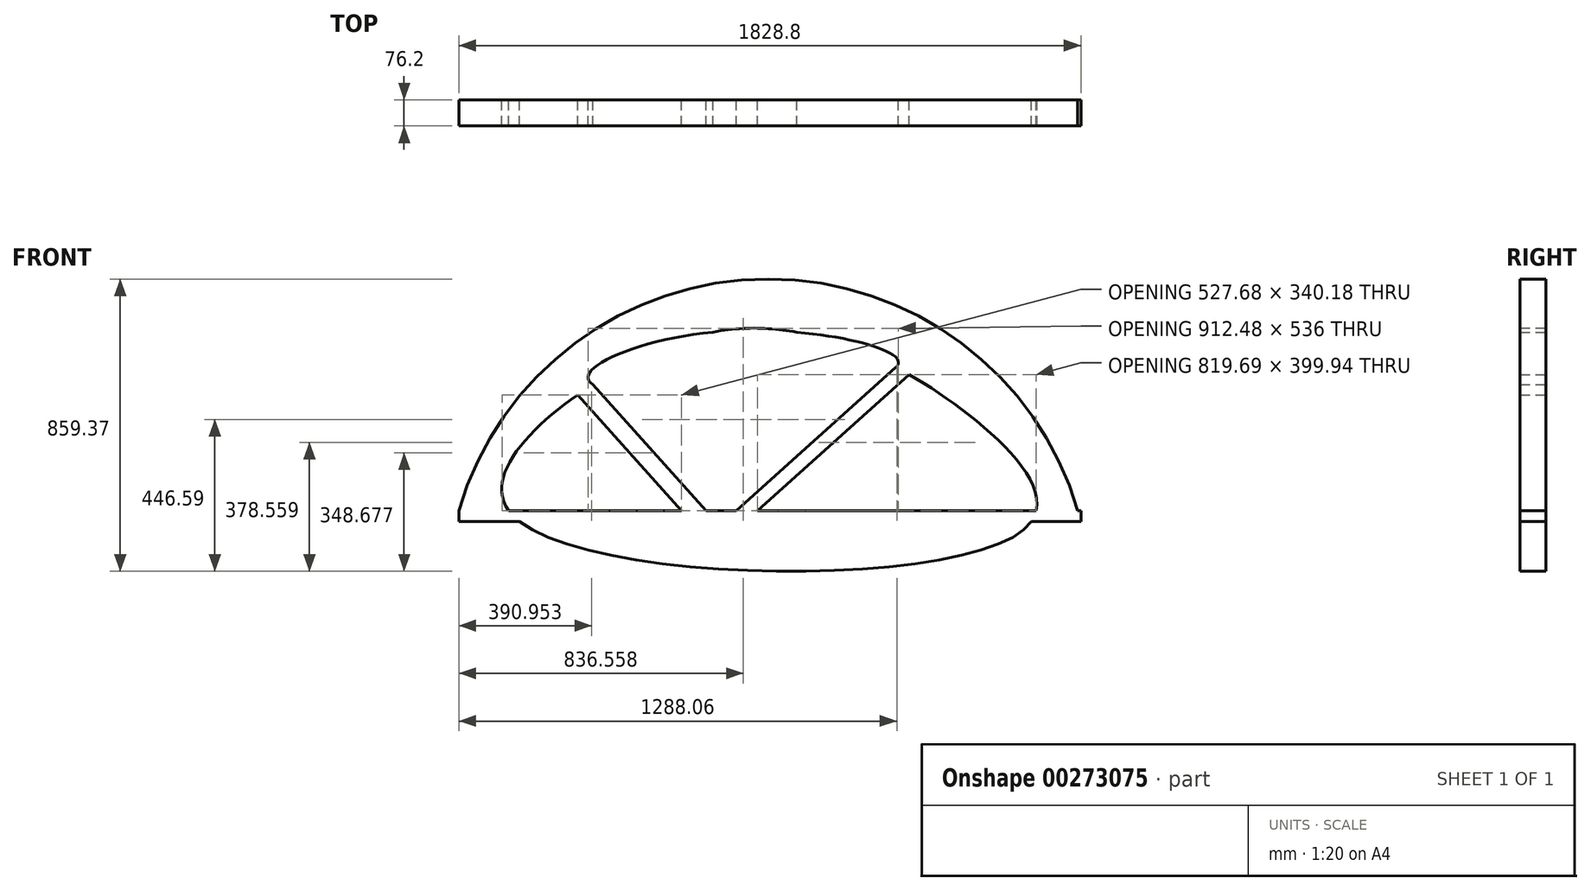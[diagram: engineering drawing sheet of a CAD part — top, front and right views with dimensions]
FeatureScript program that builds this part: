
annotation { "Feature Type Name" : "Feature", "Feature Type Description" : "" }
export const myFeature = defineFeature(function(context is Context, id is Id, definition is map)
    precondition{}
    {
        {
            var Q0;
            Q0=qCreatedBy(makeId("Front.planeOp"),FACE);
            var sketch = newSketch(context, id + "F0", { "sketchPlane" : qUnion([Q0])});
            skArc(sketch, "E0", {"start": v(891.71, -312.55) * mm, "mid": v(-18.22, 368.23) * mm, "end": v(-928.15, -312.55) * mm});
            skFitSpline(sketch, "E1", {"points": [v(-778.13, -317.3) * mm, v(-407.68, 130.46) * mm, v(83.75, 207.92) * mm, v(565.49, -26.9) * mm, v(737.38, -365.29) * mm, v(-778.13, -317.3) * mm]});
            skLineSegment(sketch, "E2", {"start": v(-111.68, -312.55) * mm, "end": v(357.16, 108.37) * mm});
            skLineSegment(sketch, "E3", {"start": v(395.54, 87.39) * mm, "end": v(-49.93, -312.55) * mm});
            skLineSegment(sketch, "E4", {"start": v(-201.38, -312.55) * mm, "end": v(-533.95, 57.88) * mm});
            skLineSegment(sketch, "E5", {"start": v(-578.76, 27.62) * mm, "end": v(-273.36, -312.55) * mm});
            skFitSpline(sketch, "E6.trimOffspring", {"points": [v(-778.13, -317.3) * mm, v(-407.68, 130.46) * mm, v(83.75, 207.92) * mm, v(565.49, -26.9) * mm, v(737.38, -365.29) * mm, v(-778.13, -317.3) * mm]});
            skFitSpline(sketch, "E7.trimOffspring", {"points": [v(-533.95, 57.88) * mm, v(-180.12, 211.97) * mm, v(357.16, 108.37) * mm, v(-533.95, 57.88) * mm]});
            skLineSegment(sketch, "E8", {"start": v(-533.95, 57.88) * mm, "end": v(-180.12, 211.97) * mm});
            skLineSegment(sketch, "E9", {"start": v(-180.12, 211.97) * mm, "end": v(357.16, 108.37) * mm});
            skLineSegment(sketch, "E10.bottom", {"start": v(-781.75, -312.55) * mm, "end": v(-273.36, -312.55) * mm});
            skLineSegment(sketch, "E10.top", {"start": v(-928.15, -345.06) * mm, "end": v(900.65, -345.06) * mm});
            skLineSegment(sketch, "E10.left", {"start": v(-928.15, -312.55) * mm, "end": v(-928.15, -345.06) * mm});
            skLineSegment(sketch, "E10.right", {"start": v(900.65, -312.55) * mm, "end": v(900.65, -345.06) * mm});
            skPoint(sketch, "E11.orphan", {"position": v(-249.24, -339.4) * mm});
            skLineSegment(sketch, "E12.trimOffspring", {"start": v(-201.38, -312.55) * mm, "end": v(-111.68, -312.55) * mm});
            skLineSegment(sketch, "E13.trimOffspring", {"start": v(-49.93, -312.55) * mm, "end": v(769.76, -312.55) * mm});
            skPoint(sketch, "E14.start.orphan", {"position": v(-79.85, -339.4) * mm});
            skLineSegment(sketch, "E15.trimOffspring", {"start": v(891.71, -312.55) * mm, "end": v(900.65, -312.55) * mm});
            skSolve(sketch);
        }
        {
            var Q0;
            Q0 = qSketchRegion(id + "F0", true);
            extrude(context, id + "F1", {"entities" : qUnion([Q0]), "depth" : 76.2 * mm});
        }
    });
